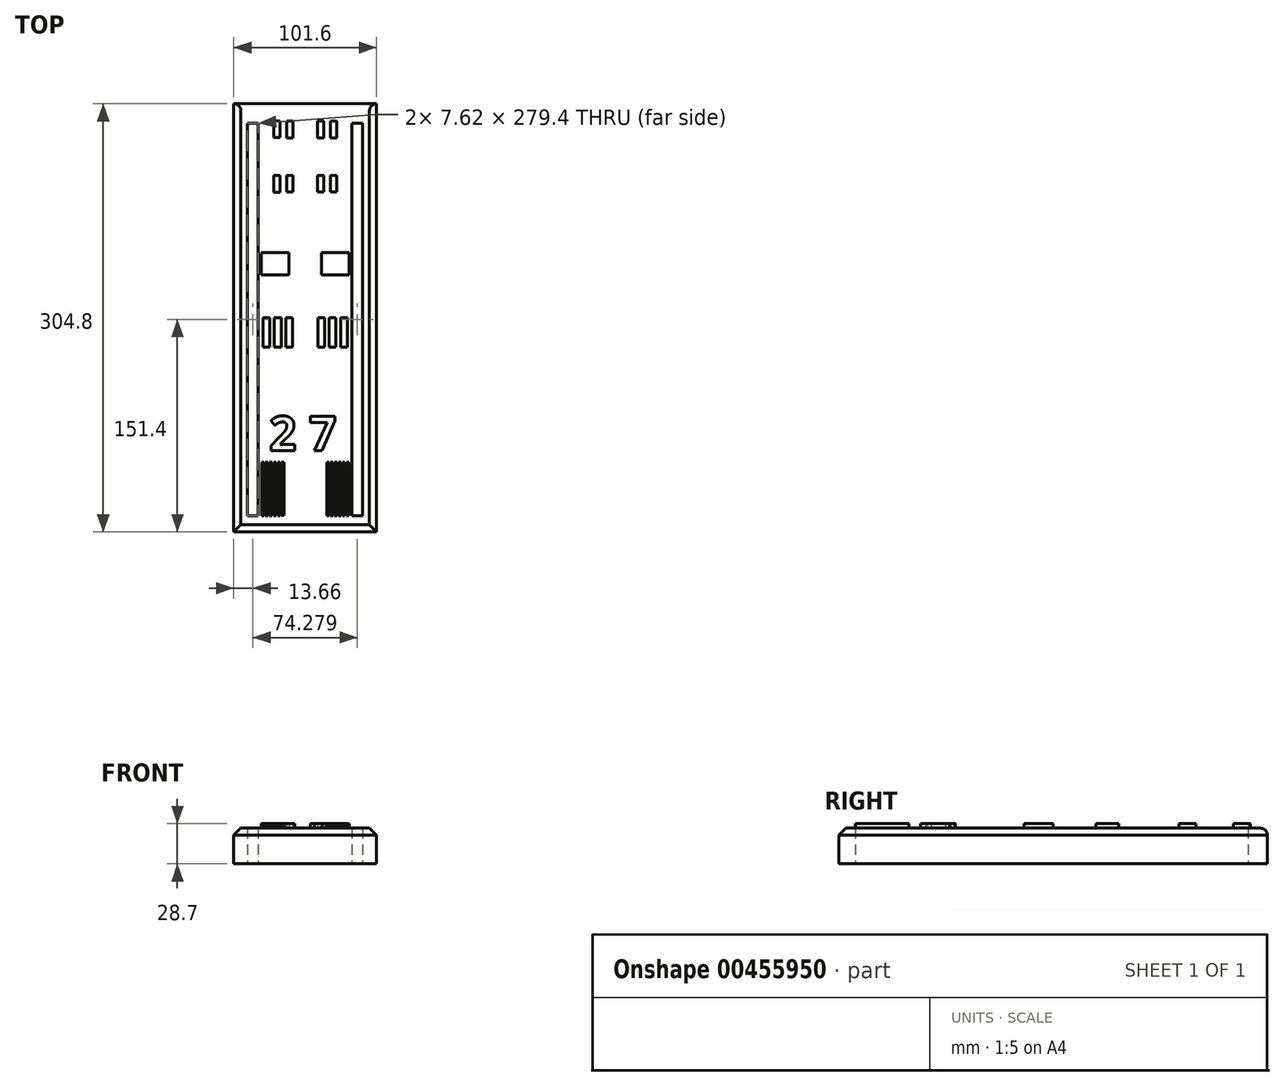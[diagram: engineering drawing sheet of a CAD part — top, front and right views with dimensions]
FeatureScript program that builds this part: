
annotation { "Feature Type Name" : "Feature", "Feature Type Description" : "" }
export const myFeature = defineFeature(function(context is Context, id is Id, definition is map)
    precondition{}
    {
        {
            var Q0;
            Q0=qCreatedBy(makeId("Top.planeOp"),FACE);
            var sketch = newSketch(context, id + "F0", { "sketchPlane" : qUnion([Q0])});
            skLineSegment(sketch, "E0", {"start": v(0, 152.4) * mm, "end": v(50.8, 152.4) * mm});
            skLineSegment(sketch, "E1", {"start": v(0, 152.4) * mm, "end": v(-50.8, 152.4) * mm});
            skLineSegment(sketch, "E2.MirrorCS", {"start": v(0, -152.4) * mm, "end": v(-50.8, -152.4) * mm});
            skLineSegment(sketch, "E3.MirrorCS", {"start": v(0, -152.4) * mm, "end": v(50.8, -152.4) * mm});
            skLineSegment(sketch, "E4", {"start": v(-50.8, 152.4) * mm, "end": v(-50.8, -152.4) * mm});
            skLineSegment(sketch, "E5", {"start": v(50.8, 152.4) * mm, "end": v(50.8, -152.4) * mm});
            skLineSegment(sketch, "E6", {"start": v(-40.95, 138.7) * mm, "end": v(-40.95, -140.7) * mm});
            skLineSegment(sketch, "E7", {"start": v(-40.95, -140.7) * mm, "end": v(-33.33, -140.7) * mm});
            skLineSegment(sketch, "E8", {"start": v(-33.33, -140.7) * mm, "end": v(-33.33, 138.7) * mm});
            skLineSegment(sketch, "E9", {"start": v(-33.33, 138.7) * mm, "end": v(-40.95, 138.7) * mm});
            skLineSegment(sketch, "E10.MirrorCS", {"start": v(33.33, -140.7) * mm, "end": v(33.33, 138.7) * mm});
            skLineSegment(sketch, "E11.MirrorCS", {"start": v(40.95, 138.7) * mm, "end": v(40.95, -140.7) * mm});
            skLineSegment(sketch, "E12.MirrorCS", {"start": v(33.33, 138.7) * mm, "end": v(40.95, 138.7) * mm});
            skLineSegment(sketch, "E13.MirrorCS", {"start": v(40.95, -140.7) * mm, "end": v(33.33, -140.7) * mm});
            skSolve(sketch);
        }
        {
            var Q0;
            Q0=makeQuery(id+"F0.imprint","IMPRINT",FACE,{"disambiguationData":[TD([[makeQuery(id+"F0.imprint","IMPRINT",EDGE,{"derivedFrom":sQuery(id+"F0.wireOp",EDGE,"E0")}),-1.0]])]});
            extrude(context, id + "F1", {"entities" : qUnion([Q0]), "depth" : 25.4 * mm});
        }
        {
            var Q0;
            Q0=makeQuery(id+"F1.opExtrude","SWEPT_FACE",FACE,{"disambiguationData":[OSD([sQuery(id+"F0.wireOp",EDGE,"E5")])]});
            var sketch = newSketch(context, id + "F2", { "sketchPlane" : qUnion([Q0])});
            skFitSpline(sketch, "E14", {"points": [v(-152.4, 25.4) * mm, v(-108.98, 35.5) * mm, v(-68.15, 25.4) * mm, v(-28.66, 34.46) * mm, v(14.2, 25.4) * mm, v(53.4, 36.44) * mm, v(86.45, 25.4) * mm, v(121.62, 35.68) * mm, v(152.4, 25.4) * mm], "startDerivative": vector(328.5, 132.6) * mm, "endDerivative": vector(264.64, -153.18) * mm});
            skSolve(sketch);
        }
        {
            var Q0;
            Q0=sQuery(id+"F2.wireOp",EDGE,"E14");
            extrude(context, id + "F3", {"bodyType" : ToolBodyType.SURFACE, "surfaceEntities" : qUnion([Q0]), "oppositeDirection" : true, "depth" : 101.6 * mm});
        }
        {
            var Q0;
            Q0=makeQuery(id+"F1.opExtrude","CAP_FACE",FACE,{"disambiguationData":[OSD([sQuery(id+"F0.wireOp",EDGE,"E0"),sQuery(id+"F0.wireOp",EDGE,"E1"),sQuery(id+"F0.wireOp",EDGE,"E2.MirrorCS"),sQuery(id+"F0.wireOp",EDGE,"E3.MirrorCS"),sQuery(id+"F0.wireOp",EDGE,"E4"),sQuery(id+"F0.wireOp",EDGE,"E5"),sQuery(id+"F0.wireOp",EDGE,"E6"),sQuery(id+"F0.wireOp",EDGE,"E7"),sQuery(id+"F0.wireOp",EDGE,"E8"),sQuery(id+"F0.wireOp",EDGE,"E9"),sQuery(id+"F0.wireOp",EDGE,"E10.MirrorCS"),sQuery(id+"F0.wireOp",EDGE,"E11.MirrorCS"),sQuery(id+"F0.wireOp",EDGE,"E12.MirrorCS"),sQuery(id+"F0.wireOp",EDGE,"E13.MirrorCS")])],"isStart":false});
            var sketch = newSketch(context, id + "F4", { "sketchPlane" : qUnion([Q0])});
            skText(sketch, "E15", { "text": "2 7", "fontName": "OpenSans-Bold.ttf"});
            skLineSegment(sketch, "E16", {"start": v(-31.04, -102.6) * mm, "end": v(-31.04, -140.7) * mm});
            skLineSegment(sketch, "E17", {"start": v(-31.04, -140.7) * mm, "end": v(-29.27, -140.7) * mm});
            skLineSegment(sketch, "E18", {"start": v(-29.27, -140.7) * mm, "end": v(-29.27, -102.6) * mm});
            skLineSegment(sketch, "E19", {"start": v(-31.04, -102.6) * mm, "end": v(-29.27, -102.6) * mm});
            skLineSegment(sketch, "E20", {"start": v(-28.25, -102.6) * mm, "end": v(-28.25, -140.7) * mm});
            skLineSegment(sketch, "E21", {"start": v(-28.25, -140.7) * mm, "end": v(-26.47, -140.7) * mm});
            skLineSegment(sketch, "E22", {"start": v(-26.47, -140.7) * mm, "end": v(-26.47, -102.6) * mm});
            skLineSegment(sketch, "E23", {"start": v(-26.47, -102.6) * mm, "end": v(-28.25, -102.6) * mm});
            skLineSegment(sketch, "E24", {"start": v(-25.46, -102.6) * mm, "end": v(-25.46, -140.7) * mm});
            skLineSegment(sketch, "E25", {"start": v(-25.46, -140.7) * mm, "end": v(-23.68, -140.7) * mm});
            skLineSegment(sketch, "E26", {"start": v(-23.68, -140.7) * mm, "end": v(-23.68, -102.6) * mm});
            skLineSegment(sketch, "E27", {"start": v(-23.68, -102.6) * mm, "end": v(-25.46, -102.6) * mm});
            skLineSegment(sketch, "E28", {"start": v(-22.4, -102.6) * mm, "end": v(-22.4, -140.7) * mm});
            skLineSegment(sketch, "E29", {"start": v(-22.4, -140.7) * mm, "end": v(-20.62, -140.7) * mm});
            skLineSegment(sketch, "E30", {"start": v(-20.62, -140.7) * mm, "end": v(-20.62, -102.6) * mm});
            skLineSegment(sketch, "E31", {"start": v(-20.62, -102.6) * mm, "end": v(-22.4, -102.6) * mm});
            skLineSegment(sketch, "E32", {"start": v(-19.6, -102.6) * mm, "end": v(-19.6, -140.7) * mm});
            skLineSegment(sketch, "E33", {"start": v(-19.6, -140.7) * mm, "end": v(-17.83, -140.7) * mm});
            skLineSegment(sketch, "E34", {"start": v(-17.83, -140.7) * mm, "end": v(-17.83, -102.6) * mm});
            skLineSegment(sketch, "E35", {"start": v(-17.83, -102.6) * mm, "end": v(-19.6, -102.6) * mm});
            skLineSegment(sketch, "E36", {"start": v(-16.81, -102.6) * mm, "end": v(-16.81, -140.7) * mm});
            skLineSegment(sketch, "E37", {"start": v(-16.81, -140.7) * mm, "end": v(-15.03, -140.65) * mm});
            skLineSegment(sketch, "E38", {"start": v(-15.03, -140.65) * mm, "end": v(-15.03, -102.6) * mm});
            skLineSegment(sketch, "E39", {"start": v(-15.03, -102.6) * mm, "end": v(-16.81, -102.6) * mm});
            skLineSegment(sketch, "E40", {"start": v(31.04, -140.7) * mm, "end": v(31.04, -102.6) * mm});
            skLineSegment(sketch, "E41", {"start": v(31.04, -102.6) * mm, "end": v(29.27, -102.6) * mm});
            skLineSegment(sketch, "E42", {"start": v(29.27, -102.6) * mm, "end": v(29.27, -140.7) * mm});
            skLineSegment(sketch, "E43", {"start": v(29.27, -140.7) * mm, "end": v(31.04, -140.7) * mm});
            skLineSegment(sketch, "E44", {"start": v(28.25, -102.6) * mm, "end": v(28.25, -140.7) * mm});
            skLineSegment(sketch, "E45", {"start": v(28.25, -140.7) * mm, "end": v(26.47, -140.7) * mm});
            skLineSegment(sketch, "E46", {"start": v(26.47, -140.7) * mm, "end": v(26.47, -102.6) * mm});
            skLineSegment(sketch, "E47", {"start": v(26.47, -102.6) * mm, "end": v(28.25, -102.6) * mm});
            skLineSegment(sketch, "E48", {"start": v(25.46, -102.6) * mm, "end": v(25.46, -140.7) * mm});
            skLineSegment(sketch, "E49", {"start": v(25.46, -140.7) * mm, "end": v(23.68, -140.7) * mm});
            skLineSegment(sketch, "E50", {"start": v(23.68, -140.7) * mm, "end": v(23.68, -102.6) * mm});
            skLineSegment(sketch, "E51", {"start": v(23.68, -102.6) * mm, "end": v(25.46, -102.6) * mm});
            skLineSegment(sketch, "E52", {"start": v(22.66, -102.6) * mm, "end": v(22.66, -140.7) * mm});
            skLineSegment(sketch, "E53", {"start": v(22.66, -140.7) * mm, "end": v(20.88, -140.7) * mm});
            skLineSegment(sketch, "E54", {"start": v(20.88, -140.7) * mm, "end": v(20.88, -102.6) * mm});
            skLineSegment(sketch, "E55", {"start": v(20.88, -102.6) * mm, "end": v(22.66, -102.6) * mm});
            skLineSegment(sketch, "E56", {"start": v(19.87, -102.6) * mm, "end": v(19.87, -140.7) * mm});
            skLineSegment(sketch, "E57", {"start": v(19.87, -140.7) * mm, "end": v(18.09, -140.7) * mm});
            skLineSegment(sketch, "E58", {"start": v(18.09, -140.7) * mm, "end": v(18.09, -102.6) * mm});
            skLineSegment(sketch, "E59", {"start": v(18.09, -102.6) * mm, "end": v(19.87, -102.6) * mm});
            skLineSegment(sketch, "E60", {"start": v(17.07, -102.6) * mm, "end": v(17.07, -140.7) * mm});
            skLineSegment(sketch, "E61", {"start": v(17.07, -140.7) * mm, "end": v(15.3, -140.7) * mm});
            skLineSegment(sketch, "E62", {"start": v(15.3, -140.7) * mm, "end": v(15.3, -102.6) * mm});
            skLineSegment(sketch, "E63", {"start": v(15.3, -102.6) * mm, "end": v(17.07, -102.6) * mm});
            skLineSegment(sketch, "E64", {"start": v(-30.03, 0) * mm, "end": v(-30.03, -20.83) * mm});
            skLineSegment(sketch, "E65", {"start": v(-30.03, -20.83) * mm, "end": v(-25.2, -20.83) * mm});
            skLineSegment(sketch, "E66", {"start": v(-25.2, -20.83) * mm, "end": v(-25.2, 0) * mm});
            skLineSegment(sketch, "E67", {"start": v(-25.2, 0) * mm, "end": v(-30.03, 0) * mm});
            skLineSegment(sketch, "E68", {"start": v(-21.9, 0) * mm, "end": v(-21.9, -20.83) * mm});
            skLineSegment(sketch, "E69", {"start": v(-21.9, -20.83) * mm, "end": v(-17.07, -20.83) * mm});
            skLineSegment(sketch, "E70", {"start": v(-17.07, -20.83) * mm, "end": v(-17.07, 0) * mm});
            skLineSegment(sketch, "E71", {"start": v(-17.07, 0) * mm, "end": v(-21.9, 0) * mm});
            skLineSegment(sketch, "E72", {"start": v(-13.77, 0) * mm, "end": v(-13.77, -20.83) * mm});
            skLineSegment(sketch, "E73", {"start": v(-13.77, -20.83) * mm, "end": v(-8.95, -20.83) * mm});
            skLineSegment(sketch, "E74", {"start": v(-8.95, -20.83) * mm, "end": v(-8.95, 0) * mm});
            skLineSegment(sketch, "E75", {"start": v(-8.95, 0) * mm, "end": v(-13.77, 0) * mm});
            skLineSegment(sketch, "E76", {"start": v(30.03, 0) * mm, "end": v(30.03, -20.83) * mm});
            skLineSegment(sketch, "E77", {"start": v(30.03, -20.83) * mm, "end": v(25.2, -20.83) * mm});
            skLineSegment(sketch, "E78", {"start": v(25.2, -20.83) * mm, "end": v(25.2, 0) * mm});
            skLineSegment(sketch, "E79", {"start": v(25.2, 0) * mm, "end": v(30.03, 0) * mm});
            skLineSegment(sketch, "E80", {"start": v(21.9, 0) * mm, "end": v(21.9, -20.83) * mm});
            skLineSegment(sketch, "E81", {"start": v(21.9, -20.83) * mm, "end": v(17.07, -20.83) * mm});
            skLineSegment(sketch, "E82", {"start": v(17.07, -20.83) * mm, "end": v(17.07, 0) * mm});
            skLineSegment(sketch, "E83", {"start": v(17.07, 0) * mm, "end": v(21.9, 0) * mm});
            skLineSegment(sketch, "E84", {"start": v(13.77, 0) * mm, "end": v(13.77, -20.83) * mm});
            skLineSegment(sketch, "E85", {"start": v(13.77, -20.83) * mm, "end": v(8.95, -20.83) * mm});
            skLineSegment(sketch, "E86", {"start": v(8.95, -20.83) * mm, "end": v(8.95, 0) * mm});
            skLineSegment(sketch, "E87", {"start": v(8.95, 0) * mm, "end": v(13.77, 0) * mm});
            skLineSegment(sketch, "E88.bottom", {"start": v(-31.3, 46.47) * mm, "end": v(-11.49, 46.47) * mm});
            skLineSegment(sketch, "E88.top", {"start": v(-31.3, 30.46) * mm, "end": v(-11.49, 30.46) * mm});
            skLineSegment(sketch, "E88.left", {"start": v(-31.3, 46.47) * mm, "end": v(-31.3, 30.46) * mm});
            skLineSegment(sketch, "E88.right", {"start": v(-11.49, 46.47) * mm, "end": v(-11.49, 30.46) * mm});
            skLineSegment(sketch, "E89.bottom", {"start": v(11.49, 46.47) * mm, "end": v(31.3, 46.47) * mm});
            skLineSegment(sketch, "E89.top", {"start": v(11.49, 30.46) * mm, "end": v(31.3, 30.46) * mm});
            skLineSegment(sketch, "E89.left", {"start": v(11.49, 46.47) * mm, "end": v(11.49, 30.46) * mm});
            skLineSegment(sketch, "E89.right", {"start": v(31.3, 46.47) * mm, "end": v(31.3, 30.46) * mm});
            skLineSegment(sketch, "E90", {"start": v(-22.4, 101.34) * mm, "end": v(-22.4, 89.4) * mm});
            skLineSegment(sketch, "E91", {"start": v(-22.4, 89.4) * mm, "end": v(-17.84, 89.4) * mm});
            skLineSegment(sketch, "E92", {"start": v(-17.84, 89.4) * mm, "end": v(-17.84, 101.34) * mm});
            skLineSegment(sketch, "E93", {"start": v(-17.84, 101.34) * mm, "end": v(-22.4, 101.34) * mm});
            skLineSegment(sketch, "E94", {"start": v(-13.26, 101.47) * mm, "end": v(-13.26, 89.53) * mm});
            skLineSegment(sketch, "E95", {"start": v(-13.26, 89.53) * mm, "end": v(-8.7, 89.53) * mm});
            skLineSegment(sketch, "E96", {"start": v(-8.7, 89.53) * mm, "end": v(-8.7, 101.47) * mm});
            skLineSegment(sketch, "E97", {"start": v(-8.7, 101.47) * mm, "end": v(-13.26, 101.47) * mm});
            skLineSegment(sketch, "E98", {"start": v(8.7, 101.47) * mm, "end": v(8.7, 89.53) * mm});
            skLineSegment(sketch, "E99", {"start": v(8.7, 89.53) * mm, "end": v(13.26, 89.53) * mm});
            skLineSegment(sketch, "E100", {"start": v(13.26, 89.53) * mm, "end": v(13.26, 101.47) * mm});
            skLineSegment(sketch, "E101", {"start": v(13.26, 101.47) * mm, "end": v(8.7, 101.47) * mm});
            skLineSegment(sketch, "E102", {"start": v(17.84, 101.47) * mm, "end": v(17.84, 89.53) * mm});
            skLineSegment(sketch, "E103", {"start": v(17.84, 89.53) * mm, "end": v(22.4, 89.53) * mm});
            skLineSegment(sketch, "E104", {"start": v(22.4, 89.53) * mm, "end": v(22.4, 101.47) * mm});
            skLineSegment(sketch, "E105", {"start": v(22.4, 101.47) * mm, "end": v(17.84, 101.47) * mm});
            skLineSegment(sketch, "E106.MirrorCS", {"start": v(-8.7, 140.08) * mm, "end": v(-8.7, 128.14) * mm});
            skLineSegment(sketch, "E107.MirrorCS", {"start": v(-8.7, 128.14) * mm, "end": v(-13.26, 128.14) * mm});
            skLineSegment(sketch, "E108.MirrorCS", {"start": v(-13.26, 140.08) * mm, "end": v(-8.7, 140.08) * mm});
            skLineSegment(sketch, "E109.MirrorCS", {"start": v(-22.4, 140.2) * mm, "end": v(-17.84, 140.2) * mm});
            skLineSegment(sketch, "E110.MirrorCS", {"start": v(-17.84, 140.2) * mm, "end": v(-17.84, 128.26) * mm});
            skLineSegment(sketch, "E111.MirrorCS", {"start": v(-22.4, 128.26) * mm, "end": v(-22.4, 140.2) * mm});
            skLineSegment(sketch, "E112.MirrorCS", {"start": v(-17.84, 128.26) * mm, "end": v(-22.4, 128.26) * mm});
            skLineSegment(sketch, "E113.MirrorCS", {"start": v(13.26, 128.14) * mm, "end": v(8.7, 128.14) * mm});
            skLineSegment(sketch, "E114.MirrorCS", {"start": v(8.7, 128.14) * mm, "end": v(8.7, 140.08) * mm});
            skLineSegment(sketch, "E115.MirrorCS", {"start": v(13.26, 140.08) * mm, "end": v(13.26, 128.14) * mm});
            skLineSegment(sketch, "E116.MirrorCS", {"start": v(17.84, 128.14) * mm, "end": v(17.84, 140.08) * mm});
            skLineSegment(sketch, "E117.MirrorCS", {"start": v(17.84, 140.08) * mm, "end": v(22.4, 140.08) * mm});
            skLineSegment(sketch, "E118.MirrorCS", {"start": v(22.4, 140.08) * mm, "end": v(22.4, 128.14) * mm});
            skLineSegment(sketch, "E119.MirrorCS", {"start": v(22.4, 128.14) * mm, "end": v(17.84, 128.14) * mm});
            skLineSegment(sketch, "E120.MirrorCS", {"start": v(-13.26, 128.14) * mm, "end": v(-13.26, 140.08) * mm});
            skLineSegment(sketch, "E121.MirrorCS", {"start": v(8.7, 140.08) * mm, "end": v(13.26, 140.08) * mm});
            const initialGuessF4  = {"E15": [-0.02572, -0.09446, 1, 0, 0.02464]};
            skSetInitialGuess(sketch, initialGuessF4);
            skSolve(sketch);
        }
        {
            var Q0;
            Q0 = qSketchRegion(id + "F4", true);
            extrude(context, id + "F5", {"entities" : qUnion([Q0]), "operationType" : NewBodyOperationType.ADD, "depth" : 3.3 * mm});
        }
        {
            var Q0;
            Q0=makeQuery(id+"F1.opExtrude","CAP_EDGE",EDGE,{"disambiguationData":[OSD([sQuery(id+"F0.wireOp",EDGE,"E5")])],"isStart":false});
            var Q1;
            Q1=makeQuery(id+"F1.opExtrude","CAP_EDGE",EDGE,{"disambiguationData":[OSD([sQuery(id+"F0.wireOp",EDGE,"E4")])],"isStart":false});
            chamfer(context, id + "F6", {"entities" : qUnion([Q0, Q1]), "width" : 5.08 * mm, "tangentPropagation" : true});
        }
        {
            var Q0;
            Q0=makeQuery(id+"F1.opExtrude","CAP_EDGE",EDGE,{"disambiguationData":[OSD([sQuery(id+"F0.wireOp",EDGE,"E2.MirrorCS"),sQuery(id+"F0.wireOp",EDGE,"E3.MirrorCS")])],"isStart":false});
            chamfer(context, id + "F7", {"entities" : qUnion([Q0]), "width" : 5.08 * mm, "tangentPropagation" : true});
        }
        {
            var Q0;
            Q0=makeQuery(id+"F1.opExtrude","CAP_EDGE",EDGE,{"disambiguationData":[OSD([sQuery(id+"F0.wireOp",EDGE,"E0"),sQuery(id+"F0.wireOp",EDGE,"E1")])],"isStart":false});
            fillet(context, id + "F8", {"entities" : qUnion([Q0]), "radius" : 5.08 * mm, "tangentPropagation" : true, "allowEdgeOverflow" : false});
        }
        {
            var Q0;
            Q0=makeQuery(id+"F3.opExtrude","SWEPT_BODY",BODY,{"disambiguationData":[OSD([sQuery(id+"F2.wireOp",EDGE,"E14")])]});
            deleteBodies(context, id + "F9", {"entities" : qUnion([Q0])});
        }
    });
